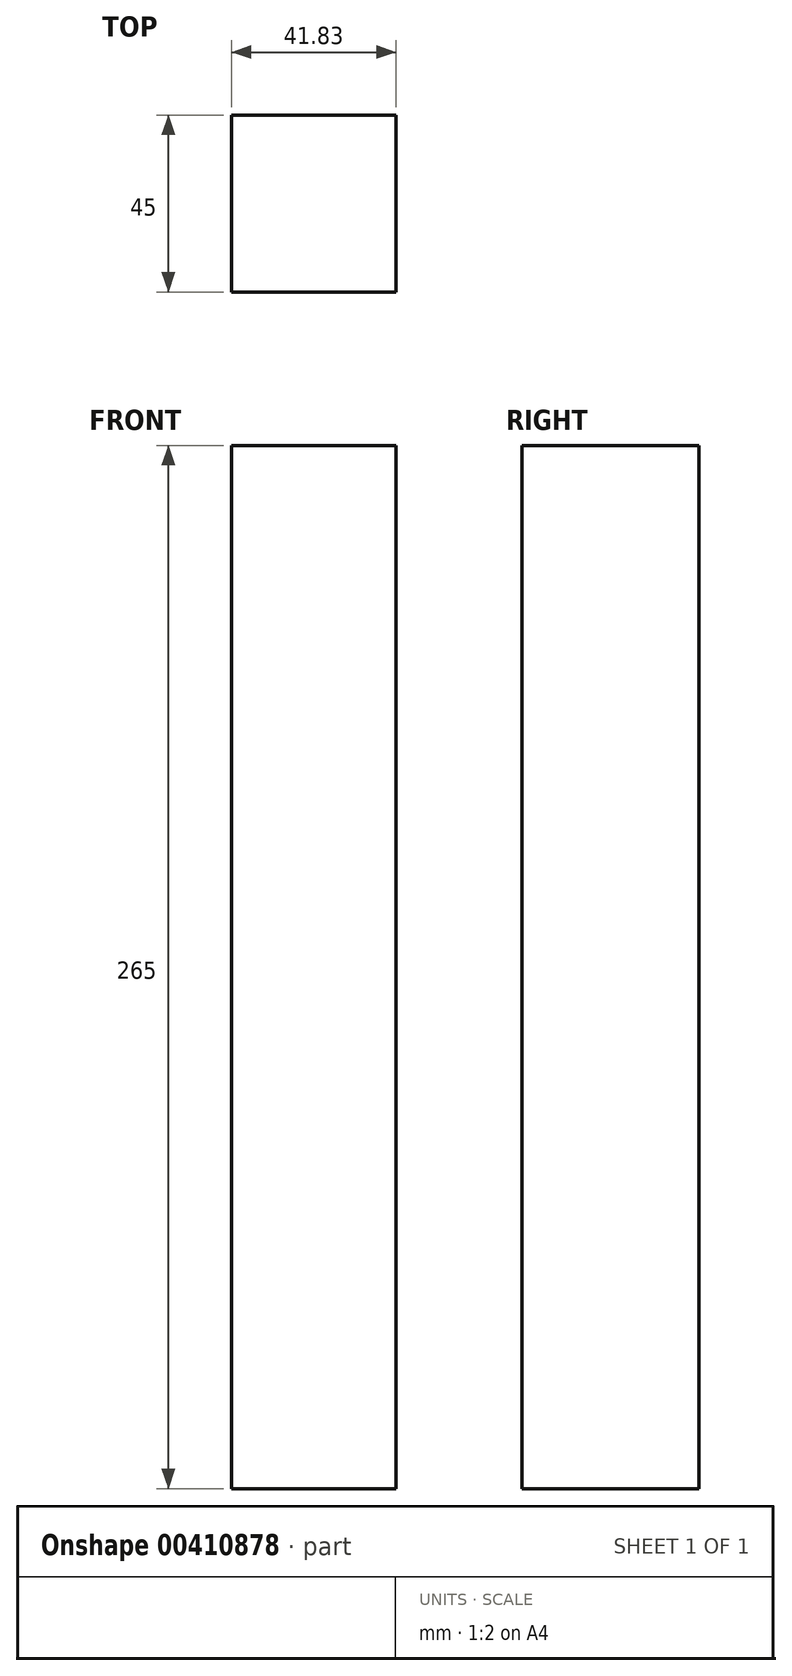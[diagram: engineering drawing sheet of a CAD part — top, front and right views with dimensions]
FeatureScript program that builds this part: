
annotation { "Feature Type Name" : "Feature", "Feature Type Description" : "" }
export const myFeature = defineFeature(function(context is Context, id is Id, definition is map)
    precondition{}
    {
        {
            var Q0;
            Q0=qCreatedBy(makeId("Top.planeOp"),FACE);
            var sketch = newSketch(context, id + "F0", { "sketchPlane" : qUnion([Q0])});
            skLineSegment(sketch, "E0.bottom", {"start": v(75.83, 34.72) * mm, "end": v(117.66, 34.72) * mm});
            skLineSegment(sketch, "E0.top", {"start": v(75.83, -10.28) * mm, "end": v(117.66, -10.28) * mm});
            skLineSegment(sketch, "E0.left", {"start": v(75.83, 34.72) * mm, "end": v(75.83, -10.28) * mm});
            skLineSegment(sketch, "E0.right", {"start": v(117.66, 34.72) * mm, "end": v(117.66, -10.28) * mm});
            skSolve(sketch);
        }
        {
            var Q0;
            Q0 = qSketchRegion(id + "F0", true);
            extrude(context, id + "F1", {"entities" : qUnion([Q0]), "depth" : 265 * mm});
        }
    });
